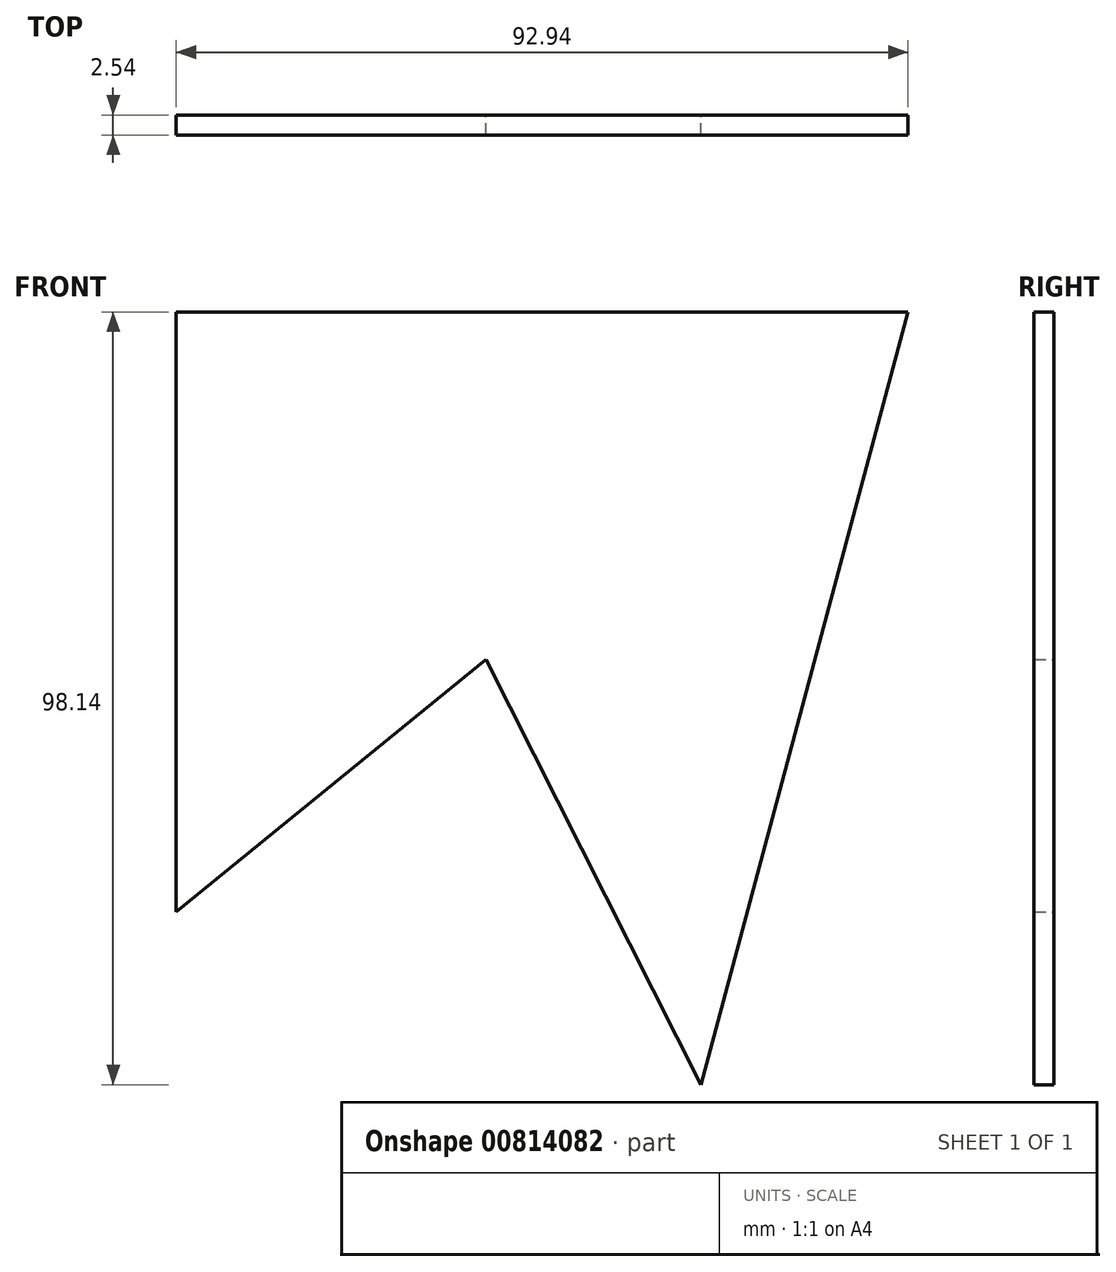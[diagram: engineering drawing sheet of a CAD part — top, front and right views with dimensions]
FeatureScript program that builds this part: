
annotation { "Feature Type Name" : "Feature", "Feature Type Description" : "" }
export const myFeature = defineFeature(function(context is Context, id is Id, definition is map)
    precondition{}
    {
        {
            var Q0;
            Q0=qCreatedBy(makeId("Front.planeOp"),FACE);
            var sketch = newSketch(context, id + "F0", { "sketchPlane" : qUnion([Q0])});
            skLineSegment(sketch, "E0", {"start": v(0, 0) * mm, "end": v(0, 76.2) * mm});
            skLineSegment(sketch, "E1", {"start": v(0, 76.2) * mm, "end": v(92.94, 76.2) * mm});
            skLineSegment(sketch, "E2", {"start": v(92.94, 76.2) * mm, "end": v(66.64, -21.94) * mm});
            skLineSegment(sketch, "E3", {"start": v(39.37, 32.1) * mm, "end": v(66.64, -21.94) * mm});
            skLineSegment(sketch, "E4", {"start": v(39.37, 32.1) * mm, "end": v(0, 0) * mm});
            skSolve(sketch);
        }
        {
            var Q0;
            Q0 = qSketchRegion(id + "F0", true);
            extrude(context, id + "F1", {"entities" : qUnion([Q0]), "depth" : 2.54 * mm, "offsetDistance" : 25.4 * mm});
        }
    });
